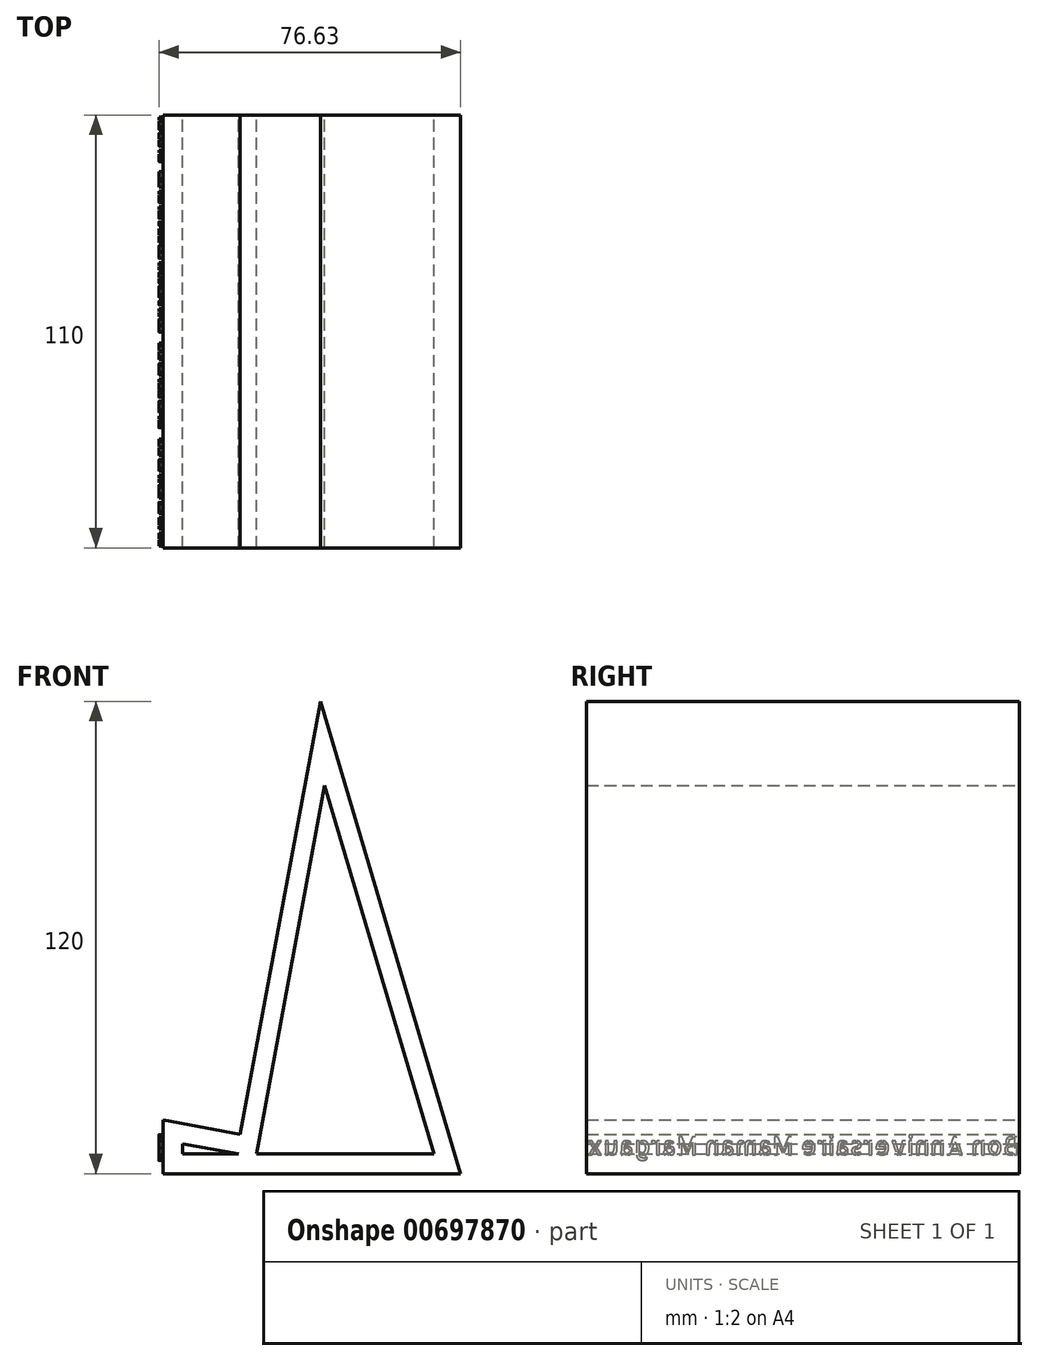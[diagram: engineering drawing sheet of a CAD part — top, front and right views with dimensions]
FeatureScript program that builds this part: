
annotation { "Feature Type Name" : "Feature", "Feature Type Description" : "" }
export const myFeature = defineFeature(function(context is Context, id is Id, definition is map)
    precondition{}
    {
        {
            var Q0;
            Q0=qCreatedBy(makeId("Front.planeOp"),FACE);
            var sketch = newSketch(context, id + "F0", { "sketchPlane" : qUnion([Q0])});
            skLineSegment(sketch, "E0", {"start": v(0, 0) * mm, "end": v(-40, 0) * mm});
            skLineSegment(sketch, "E1", {"start": v(-40, 13.64) * mm, "end": v(-40, 0) * mm});
            skLineSegment(sketch, "E2", {"start": v(-40, 13.64) * mm, "end": v(-20.33, 10) * mm});
            skLineSegment(sketch, "E3", {"start": v(-20.33, 10) * mm, "end": v(0, 120) * mm});
            skLineSegment(sketch, "E4", {"start": v(0, 120) * mm, "end": v(35.63, 0) * mm});
            skLineSegment(sketch, "E5", {"start": v(35.63, 0) * mm, "end": v(0, 0) * mm});
            skLineSegment(sketch, "E6.0", {"start": v(-35, 7.63) * mm, "end": v(-20.8, 5) * mm});
            skLineSegment(sketch, "E6.1", {"start": v(-35, 7.63) * mm, "end": v(-35, 5) * mm});
            skLineSegment(sketch, "E6.2", {"start": v(-20.8, 5) * mm, "end": v(-35, 5) * mm});
            skLineSegment(sketch, "E6.3", {"start": v(0, 5) * mm, "end": v(-16.17, 5) * mm});
            skLineSegment(sketch, "E6.4", {"start": v(-16.17, 5) * mm, "end": v(1.13, 98.62) * mm});
            skLineSegment(sketch, "E6.5", {"start": v(28.93, 5) * mm, "end": v(0, 5) * mm});
            skLineSegment(sketch, "E6.6", {"start": v(1.13, 98.62) * mm, "end": v(28.93, 5) * mm});
            skSolve(sketch);
        }
        {
            var Q0;
            Q0 = qSketchRegion(id + "F0", true);
            extrude(context, id + "F1", {"entities" : qUnion([Q0]), "depth" : 110 * mm, "offsetDistance" : 25.4 * mm});
        }
        {
            var Q0;
            Q0=makeQuery(id+"F1.opExtrude","SWEPT_FACE",FACE,{"disambiguationData":[OSD([sQuery(id+"F0.wireOp",EDGE,"E1")])]});
            var sketch = newSketch(context, id + "F2", { "sketchPlane" : qUnion([Q0])});
            skText(sketch, "E7", { "text": "Bon Anniversaire Maman Margaux", "fontName": "AllertaStencil-Regular.ttf"});
            skPoint(sketch, "E8", {"position": v(55, 0) * mm});
            const initialGuessF2  = {"E7": [0, 0.00478, 1, 0, 0.00462]};
            skSetInitialGuess(sketch, initialGuessF2);
            skSolve(sketch);
        }
        {
            var Q0;
            Q0 = qSketchRegion(id + "F2", true);
            extrude(context, id + "F3", {"entities" : qUnion([Q0]), "operationType" : NewBodyOperationType.ADD, "depth" : 1 * mm, "offsetDistance" : 25.4 * mm});
        }
    });
